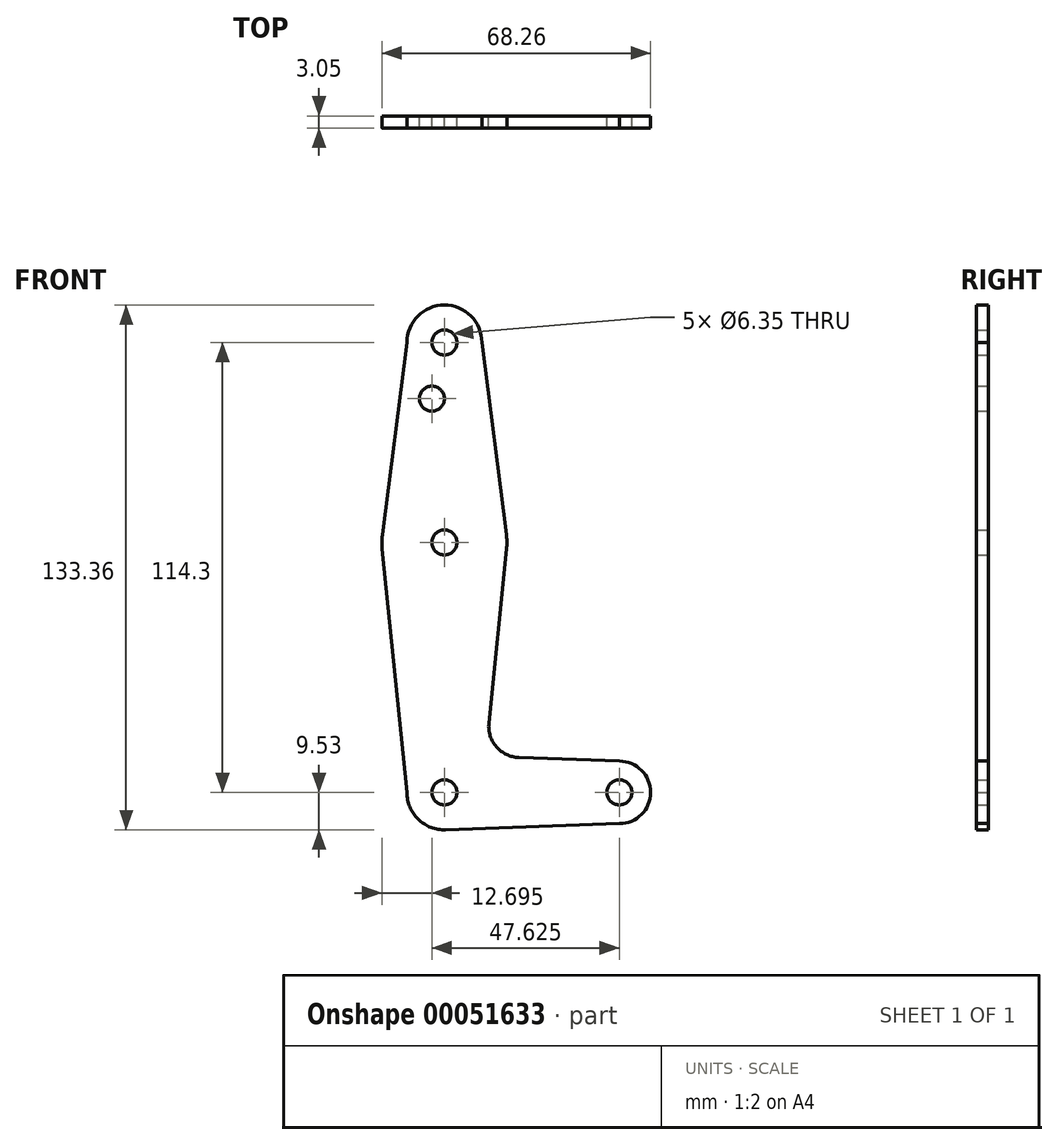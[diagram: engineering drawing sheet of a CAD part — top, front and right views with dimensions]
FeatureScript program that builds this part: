
annotation { "Feature Type Name" : "Feature", "Feature Type Description" : "" }
export const myFeature = defineFeature(function(context is Context, id is Id, definition is map)
    precondition{}
    {
        {
            var Q0;
            Q0=qCreatedBy(makeId("Front.planeOp"),FACE);
            var sketch = newSketch(context, id + "F0", { "sketchPlane" : qUnion([Q0])});
            skLineSegment(sketch, "E0", {"start": v(44.45, 0) * mm, "end": v(0, 0) * mm, "construction": true});
            skLineSegment(sketch, "E1", {"start": v(0, 0) * mm, "end": v(0, 114.3) * mm, "construction": true});
            skCircle(sketch, "E2", {"center": v(0, 114.3) * mm, "radius": 9.53 * mm});
            skCircle(sketch, "E3", {"center": v(0, 0) * mm, "radius": 9.53 * mm});
            skCircle(sketch, "E4", {"center": v(44.45, 0) * mm, "radius": 7.94 * mm});
            skCircle(sketch, "E5", {"center": v(0, 63.5) * mm, "radius": 15.88 * mm});
            skLineSegment(sketch, "E6", {"start": v(9.52, 114.3) * mm, "end": v(15.75, 65.5) * mm});
            skLineSegment(sketch, "E7", {"start": v(11.3, 17.6) * mm, "end": v(15.8, 61.9) * mm});
            skLineSegment(sketch, "E8", {"start": v(-9.52, 0) * mm, "end": v(-15.8, 61.9) * mm});
            skLineSegment(sketch, "E9", {"start": v(-9.52, 114.3) * mm, "end": v(-15.75, 65.5) * mm});
            skLineSegment(sketch, "E10", {"start": v(44.45, -7.94) * mm, "end": v(0, -9.53) * mm});
            skLineSegment(sketch, "E11", {"start": v(44.45, 7.94) * mm, "end": v(18.93, 8.85) * mm});
            skCircle(sketch, "E12", {"center": v(0, 114.3) * mm, "radius": 3.18 * mm});
            skCircle(sketch, "E13", {"center": v(0, 63.5) * mm, "radius": 3.18 * mm});
            skCircle(sketch, "E14", {"center": v(0, 0) * mm, "radius": 3.18 * mm});
            skCircle(sketch, "E15", {"center": v(44.45, 0) * mm, "radius": 3.18 * mm});
            skCircle(sketch, "E16", {"center": v(-3.18, 100.03) * mm, "radius": 3.18 * mm});
            skArc(sketch, "E17.filletArc", {"start": v(11.3, 17.6) * mm, "mid": v(13.22, 11.57) * mm, "end": v(18.93, 8.85) * mm});
            skSolve(sketch);
        }
        {
            var Q0;
            Q0 = qSketchRegion(id + "F0", true);
            extrude(context, id + "F1", {"entities" : qUnion([Q0]), "depth" : 3.05 * mm});
        }
    });
